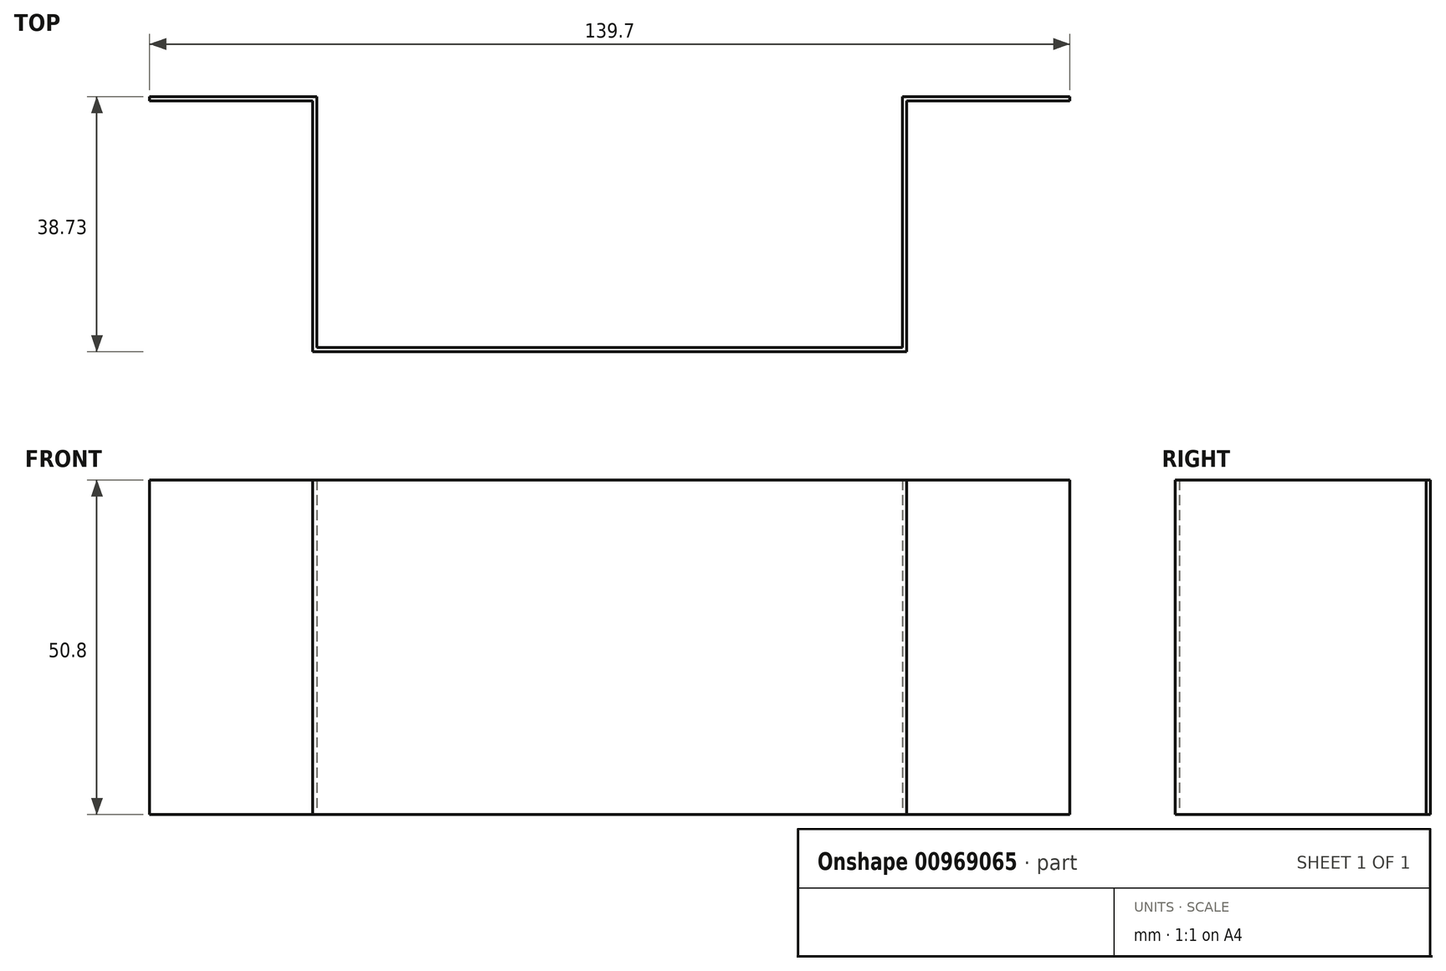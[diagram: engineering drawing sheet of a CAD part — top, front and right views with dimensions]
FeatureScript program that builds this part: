
annotation { "Feature Type Name" : "Feature", "Feature Type Description" : "" }
export const myFeature = defineFeature(function(context is Context, id is Id, definition is map)
    precondition{}
    {
        {
            var Q0;
            Q0=qCreatedBy(makeId("Top.planeOp"),FACE);
            var sketch = newSketch(context, id + "F0", { "sketchPlane" : qUnion([Q0])});
            skLineSegment(sketch, "E0", {"start": v(0, 0) * mm, "end": v(25.4, 0) * mm});
            skLineSegment(sketch, "E1", {"start": v(25.4, 0) * mm, "end": v(25.4, -38.1) * mm});
            skLineSegment(sketch, "E2", {"start": v(25.4, -38.1) * mm, "end": v(114.3, -38.1) * mm});
            skLineSegment(sketch, "E3", {"start": v(114.3, -38.1) * mm, "end": v(114.3, 0) * mm});
            skLineSegment(sketch, "E4", {"start": v(114.3, 0) * mm, "end": v(139.7, 0) * mm});
            skLineSegment(sketch, "E5.0", {"start": v(114.94, -0.64) * mm, "end": v(139.7, -0.64) * mm});
            skLineSegment(sketch, "E5.1", {"start": v(0, -0.63) * mm, "end": v(24.77, -0.63) * mm});
            skLineSegment(sketch, "E5.2", {"start": v(24.77, -0.63) * mm, "end": v(24.77, -38.74) * mm});
            skLineSegment(sketch, "E5.3", {"start": v(24.77, -38.74) * mm, "end": v(114.94, -38.74) * mm});
            skLineSegment(sketch, "E5.4", {"start": v(114.94, -38.74) * mm, "end": v(114.94, -0.64) * mm});
            skLineSegment(sketch, "E6", {"start": v(0, 0) * mm, "end": v(0, -0.63) * mm});
            skLineSegment(sketch, "E7", {"start": v(139.7, 0) * mm, "end": v(139.7, -0.64) * mm});
            skSolve(sketch);
        }
        {
            var Q0;
            Q0 = qSketchRegion(id + "F0", true);
            extrude(context, id + "F1", {"entities" : qUnion([Q0]), "depth" : 50.8 * mm, "offsetDistance" : 25.4 * mm});
        }
    });
